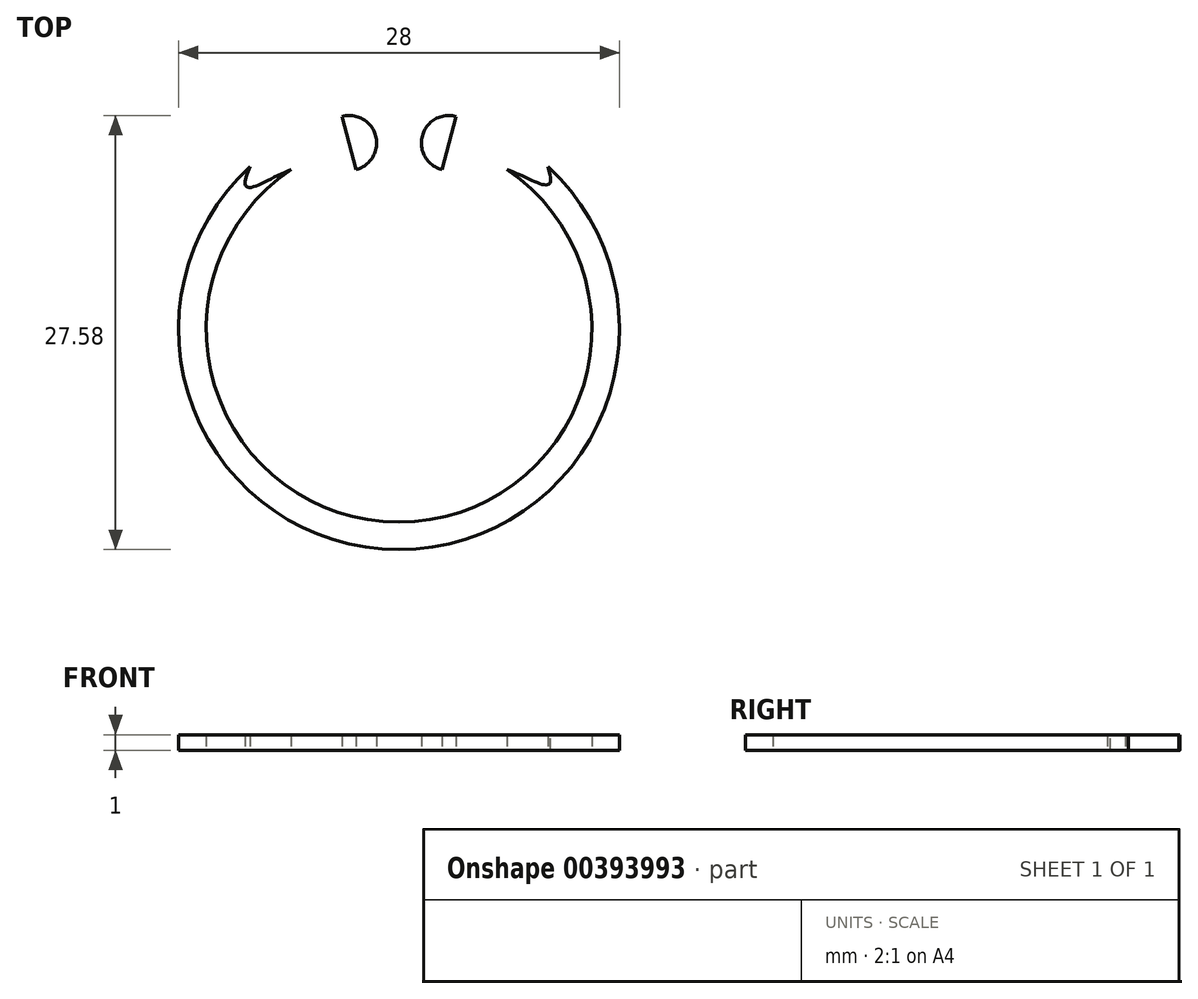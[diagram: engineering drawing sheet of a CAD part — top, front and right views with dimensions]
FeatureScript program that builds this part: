
annotation { "Feature Type Name" : "Feature", "Feature Type Description" : "" }
export const myFeature = defineFeature(function(context is Context, id is Id, definition is map)
    precondition{}
    {
        {
            var Q0;
            Q0=qCreatedBy(makeId("Top.planeOp"),FACE);
            var sketch = newSketch(context, id + "F0", { "sketchPlane" : qUnion([Q0])});
            skArc(sketch, "E0", {"start": v(-6.87, 10.14) * mm, "mid": v(0, -12.25) * mm, "end": v(6.87, 10.14) * mm});
            skArc(sketch, "E1", {"start": v(-3.62, 13.52) * mm, "mid": v(0, -14) * mm, "end": v(3.62, 13.52) * mm});
            skLineSegment(sketch, "E2", {"start": v(0, 0) * mm, "end": v(0, 20) * mm, "construction": true});
            skLineSegment(sketch, "E3", {"start": v(-2.72, 10.14) * mm, "end": v(-3.62, 13.52) * mm});
            skLineSegment(sketch, "E4", {"start": v(2.72, 10.14) * mm, "end": v(3.62, 13.52) * mm});
            skArc(sketch, "E5", {"start": v(-3.62, 13.52) * mm, "mid": v(-1.48, 12.29) * mm, "end": v(-2.72, 10.14) * mm});
            skArc(sketch, "E6", {"start": v(3.62, 13.52) * mm, "mid": v(1.48, 12.29) * mm, "end": v(2.72, 10.14) * mm});
            skFitSpline(sketch, "E7", {"points": [v(2.72, 10.14) * mm, v(6.87, 10.14) * mm, v(9.45, 10.33) * mm], "startDerivative": vector(5.67, -1.9) * mm, "endDerivative": vector(-5.43, 14.98) * mm});
            skFitSpline(sketch, "E8", {"points": [v(-2.72, 10.14) * mm, v(-6.87, 10.14) * mm, v(-9.45, 10.33) * mm], "startDerivative": vector(-7.45, -2.59) * mm, "endDerivative": vector(7.98, 17.22) * mm});
            skSolve(sketch);
        }
        {
            var Q0;
            Q0=makeQuery(id+"F0.imprint","IMPRINT",FACE,{"disambiguationData":[TD([[makeQuery(id+"F0.imprint","IMPRINT",EDGE,{"derivedFrom":sQuery(id+"F0.wireOp",EDGE,"E4")}),1.0]])]});
            var Q1;
            Q1=makeQuery(id+"F0.imprint","IMPRINT",FACE,{"disambiguationData":[TD([[makeQuery(id+"F0.imprint","IMPRINT",EDGE,{"derivedFrom":sQuery(id+"F0.wireOp",EDGE,"E3")}),-1.0]])]});
            var Q2;
            Q2=makeQuery(id+"F0.imprint","IMPRINT",FACE,{"disambiguationData":[TD([[makeQuery(id+"F0.imprint","IMPRINT",EDGE,{"derivedFrom":sQuery(id+"F0.wireOp",EDGE,"E0")}),-1.0]])]});
            extrude(context, id + "F1", {"entities" : qUnion([Q0, Q1, Q2]), "depth" : 1 * mm});
        }
        {
            var Q0;
            Q0=sQuery(id+"F0.wireOp",VERTEX,"E5.center");
            var Q1;
            Q1=sQuery(id+"F0.wireOp",VERTEX,"E6.center");
            var Q2;
            Q2=makeQuery(id+"F1.opExtrude","SWEPT_BODY",BODY,{"disambiguationData":[OSD([sQuery(id+"F0.wireOp",EDGE,"E0"),sQuery(id+"F0.wireOp",EDGE,"E1"),sQuery(id+"F0.wireOp",EDGE,"E5"),sQuery(id+"F0.wireOp",EDGE,"E6"),sQuery(id+"F0.wireOp",EDGE,"E7"),sQuery(id+"F0.wireOp",EDGE,"E8")])]});
            hole(context, id + "F2", {"style" : HoleStyle.SIMPLE, "endStyle" : HoleEndStyle.BLIND, "oppositeDirection" : true, "holeDiameter" : .5 * mm, "holeDepth" : 17 * mm, "isTappedThrough" : true, "tappedDepth" : 12 * mm, "tapClearance" : 3, "locations" : qUnion([Q0, Q1]), "scope" : qUnion([Q2])});
        }
    });
